# Revit family: RN 85130 Optiflex-Profix-Übergang
name_source: partatom
category: Rohrformteile
units: mm (PartAtom-declared; Revit-internal decimal feet)

## family parameters
Arbeitsebenenbasiert = Nein
Beim Laden mit Abzugskörper schneiden = Nein
Bemaßung runder Anschluss = Durchmesser verwenden
Gemeinsam genutzt = Nein
Immer vertikal = Ja
Teiletyp = Verbindung

## types (6) — shared parameters
1.010.00.2 Blattnummer der Richtlinie = 29
1.010.00.3 Ausgabedatum (Monat) der Richtlinie = 201308
1.010.00.4 Herstellername = R. Nussbaum AG
1.010.00.5 Revisionsdatum der Datei = 20190521
1.010.00.6 Webadresse des Herstellers = http://www.nussbaum.ch
1.100.00.4 Produktbezeichnung = Versorgung
1.110.00.2 Index = 5
1.110.00.4 Produktbezeichnung = Optiflex
1.960/3L.00.8 Link (URL) = https://www.nussbaum.ch
29.700.00.4 Produktname = Optiflex-Profix-Übergang, mit Aussengewinde
29.700.00.5 Produktkennung = 2
29.700.00.6 Querschnittsform = 1
29.700.00.7 Nennweitensystem = DN
29.700.00.8 Nenndrucksystem = PN
29.710.02.4 Nenndruck = 10
29.710.02.5 max. zul. Überdruck [hPa] = 1000
29.710.02.7 max. zul. Dauer-Betriebsdruck [hPa] = 1000
29.710.02.9 max. zul. Dauer-Betriebstemperatur [°C] = 70
Connector Visibility = Nein
EnclosingSpace Visibility = Nein
Hersteller = R. Nussbaum AG
R. Nussbaum AG 85130.24 de Visibility = Nein
R. Nussbaum AG 85130.26 de Visibility = Nein
URL = https://www.nussbaum.ch

## per-type parameters (varying)
| type | 1.800.00.3 TGA-Nummer | 1.800.00.4 Kommentarfeld | 1.810.00.3 Hersteller-Bestellnummer | 1.810.00.4 DATANORM-Nummer | 1.810.00.5 StLB-Nummer | 1.810.00.6 GTIN-Nummer | 29.710.02.10 Formstück-Gewicht [kg] | 29.710.02.3 Benennung | CONNECTOR0_DIAMETER_dX_0r | CONNECTOR0_dX_01 | CONNECTOR0_ref_dX | CONNECTOR1_DIAMETER_dX_0r | CONNECTOR1_dX_00 | CONNECTOR1_dX_01 | CONNECTOR1_ref_dX | Modell | R. Nussbaum AG 85130.21 de Visibility | R. Nussbaum AG 85130.22 de Visibility | R. Nussbaum AG 85130.23 de Visibility | R. Nussbaum AG 85130.27 de Visibility | Typenkommentare |
| DN=25x20 | 01900500000000000000000000000000000000000000000049000000000000000006 | 85130.27, Optiflex-Profix-Übergang, mit Aussengewinde, DN=25x20, L=74, R=1 | 85130.27 | 85130.27 | 322.133 | 7612945698056 | 0.204 | Optiflex-Profix-Übergang, mit Aussengewinde, DN=25x20, L=74, R=1 | 25 mm  [stored 0.082021 ft] | 17 mm | 17 mm | 20 mm | 32 mm | 74 mm | 32 mm | 85130.27 | Nein | Nein | Nein | Ja | Optiflex-Profix-Übergang  DN=25x20 |
| DN=20x15 | 01900500000000000000000000000000000000000000000049000000000000000003 | 85130.23, Optiflex-Profix-Übergang, mit Aussengewinde, DN=20x15, L=65, R=¾ | 85130.23 | 85130.23 | 332.122 | 7612945686466 | 0.119 | Optiflex-Profix-Übergang, mit Aussengewinde, DN=20x15, L=65, R=¾ | 20 mm | 15 mm | 15 mm | 15 mm | 31 mm | 65 mm | 31 mm | 85130.23 | Nein | Nein | Ja | Nein | Optiflex-Profix-Übergang  DN=20x15 |
| DN=15 | 01900500000000000000000000000000000000000000000049000000000000000002 | 85130.22, Optiflex-Profix-Übergang, mit Aussengewinde, DN=15, L=65, R=½ | 85130.22 | 85130.22 | 332.112 | 7612945686459 | 0.109 | Optiflex-Profix-Übergang, mit Aussengewinde, DN=15, L=65, R=½ | 15 mm | 13 mm | 13 mm | 15 mm | 31 mm | 65 mm | 31 mm | 85130.22 | Nein | Ja | Nein | Nein | Optiflex-Profix-Übergang  DN=15 |
| DN=12x15 | 01900500000000000000000000000000000000000000000049000000000000000001 | 85130.21, Optiflex-Profix-Übergang, mit Aussengewinde, DN=12x15, L=64, R=½ | 85130.21 | 85130.21 | 332.111 | 7612945686442 | 0.093 | Optiflex-Profix-Übergang, mit Aussengewinde, DN=12x15, L=64, R=½ | 15 mm | 13 mm | 13 mm | 12 mm  [stored 0.0393701 ft] | 30 mm | 64 mm | 30 mm | 85130.21 | Ja | Nein | Nein | Nein | Optiflex-Profix-Übergang  DN=12x15 |
| DN=20x2 | 01900500000000000000000000000000000000000000000049000000000000000003 | 85130.23, Optiflex-Profix-Übergang, mit Aussengewinde, DN=20x15, L=65, R=¾ | 85130.23 | 85130.23 | 332.122 | 7612945686466 | 0.119 | Optiflex-Profix-Übergang, mit Aussengewinde, DN=20x15, L=65, R=¾ | 20 mm | 15 mm | 15 mm | 15 mm | 31 mm | 65 mm | 31 mm | 85130.23 | Nein | Nein | Ja | Nein | Optiflex-Profix-Übergang  DN=20x15 |
| DN=20x1 | 01900500000000000000000000000000000000000000000049000000000000000003 | 85130.23, Optiflex-Profix-Übergang, mit Aussengewinde, DN=20x15, L=65, R=¾ | 85130.23 | 85130.23 | 332.122 | 7612945686466 | 0.119 | Optiflex-Profix-Übergang, mit Aussengewinde, DN=20x15, L=65, R=¾ | 20 mm | 15 mm | 15 mm | 15 mm | 31 mm | 65 mm | 31 mm | 85130.23 | Nein | Nein | Ja | Nein | Optiflex-Profix-Übergang  DN=20x15 |

note: [stored X ft] marks values corroborated as IEEE doubles in the binary element streams (Revit-internal decimal feet)

## geometry (parser evidence)
native form markers: Sweep x1
no freeform markers — native parametric forms only
